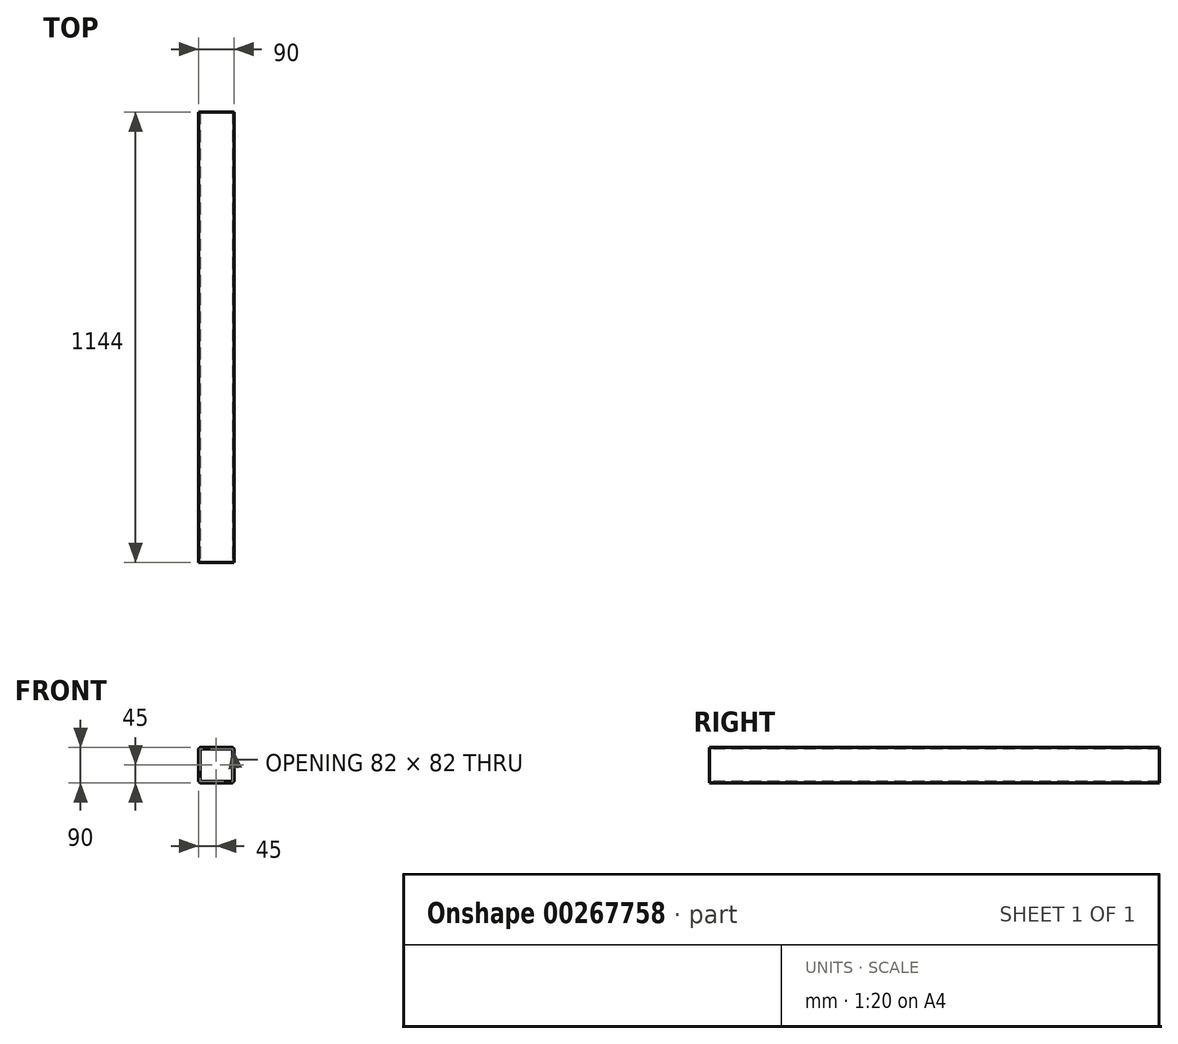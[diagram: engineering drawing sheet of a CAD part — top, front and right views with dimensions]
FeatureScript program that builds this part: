
annotation { "Feature Type Name" : "Feature", "Feature Type Description" : "" }
export const myFeature = defineFeature(function(context is Context, id is Id, definition is map)
    precondition{}
    {
        {
            var Q0;
            Q0=qCreatedBy(makeId("Front.planeOp"),FACE);
            var sketch = newSketch(context, id + "F0", { "sketchPlane" : qUnion([Q0])});
            skLineSegment(sketch, "E0.bottom", {"start": v(39, 45) * mm, "end": v(-39, 45) * mm});
            skLineSegment(sketch, "E0.top", {"start": v(39, -45) * mm, "end": v(-39, -45) * mm});
            skLineSegment(sketch, "E0.left", {"start": v(45, 39) * mm, "end": v(45, -39) * mm});
            skLineSegment(sketch, "E0.right", {"start": v(-45, 39) * mm, "end": v(-45, -39) * mm});
            skPoint(sketch, "E0.middle", {"position": v(0, 0) * mm});
            skPoint(sketch, "E1.visualSharp", {"position": v(-45, 45) * mm});
            skArc(sketch, "E1.filletArc", {"start": v(-39, 45) * mm, "mid": v(-43.24, 43.24) * mm, "end": v(-45, 39) * mm});
            skPoint(sketch, "E2.visualSharp", {"position": v(45, 45) * mm});
            skArc(sketch, "E2.filletArc", {"start": v(45, 39) * mm, "mid": v(43.24, 43.24) * mm, "end": v(39, 45) * mm});
            skPoint(sketch, "E3.visualSharp", {"position": v(45, -45) * mm});
            skArc(sketch, "E3.filletArc", {"start": v(39, -45) * mm, "mid": v(43.24, -43.24) * mm, "end": v(45, -39) * mm});
            skPoint(sketch, "E4.visualSharp", {"position": v(-45, -45) * mm});
            skArc(sketch, "E4.filletArc", {"start": v(-45, -39) * mm, "mid": v(-43.24, -43.24) * mm, "end": v(-39, -45) * mm});
            skArc(sketch, "E5.0", {"start": v(-39, 41) * mm, "mid": v(-40.41, 40.41) * mm, "end": v(-41, 39) * mm});
            skLineSegment(sketch, "E5.1", {"start": v(39, 41) * mm, "end": v(-39, 41) * mm});
            skLineSegment(sketch, "E5.2", {"start": v(-41, 39) * mm, "end": v(-41, -39) * mm});
            skArc(sketch, "E5.3", {"start": v(41, 39) * mm, "mid": v(40.41, 40.41) * mm, "end": v(39, 41) * mm});
            skArc(sketch, "E5.4", {"start": v(-41, -39) * mm, "mid": v(-40.41, -40.41) * mm, "end": v(-39, -41) * mm});
            skLineSegment(sketch, "E5.5", {"start": v(39, -41) * mm, "end": v(-39, -41) * mm});
            skArc(sketch, "E5.6", {"start": v(39, -41) * mm, "mid": v(40.41, -40.41) * mm, "end": v(41, -39) * mm});
            skLineSegment(sketch, "E5.7", {"start": v(41, 39) * mm, "end": v(41, -39) * mm});
            skSolve(sketch);
        }
        {
            var Q0;
            Q0=makeQuery(id+"F0.imprint","IMPRINT",FACE,{"disambiguationData":[TD([[makeQuery(id+"F0.imprint","IMPRINT",EDGE,{"derivedFrom":sQuery(id+"F0.wireOp",EDGE,"E0.bottom")}),1.0]])]});
            extrude(context, id + "F1", {"entities" : qUnion([Q0]), "oppositeDirection" : true, "depth" : 1144 * mm});
        }
    });
